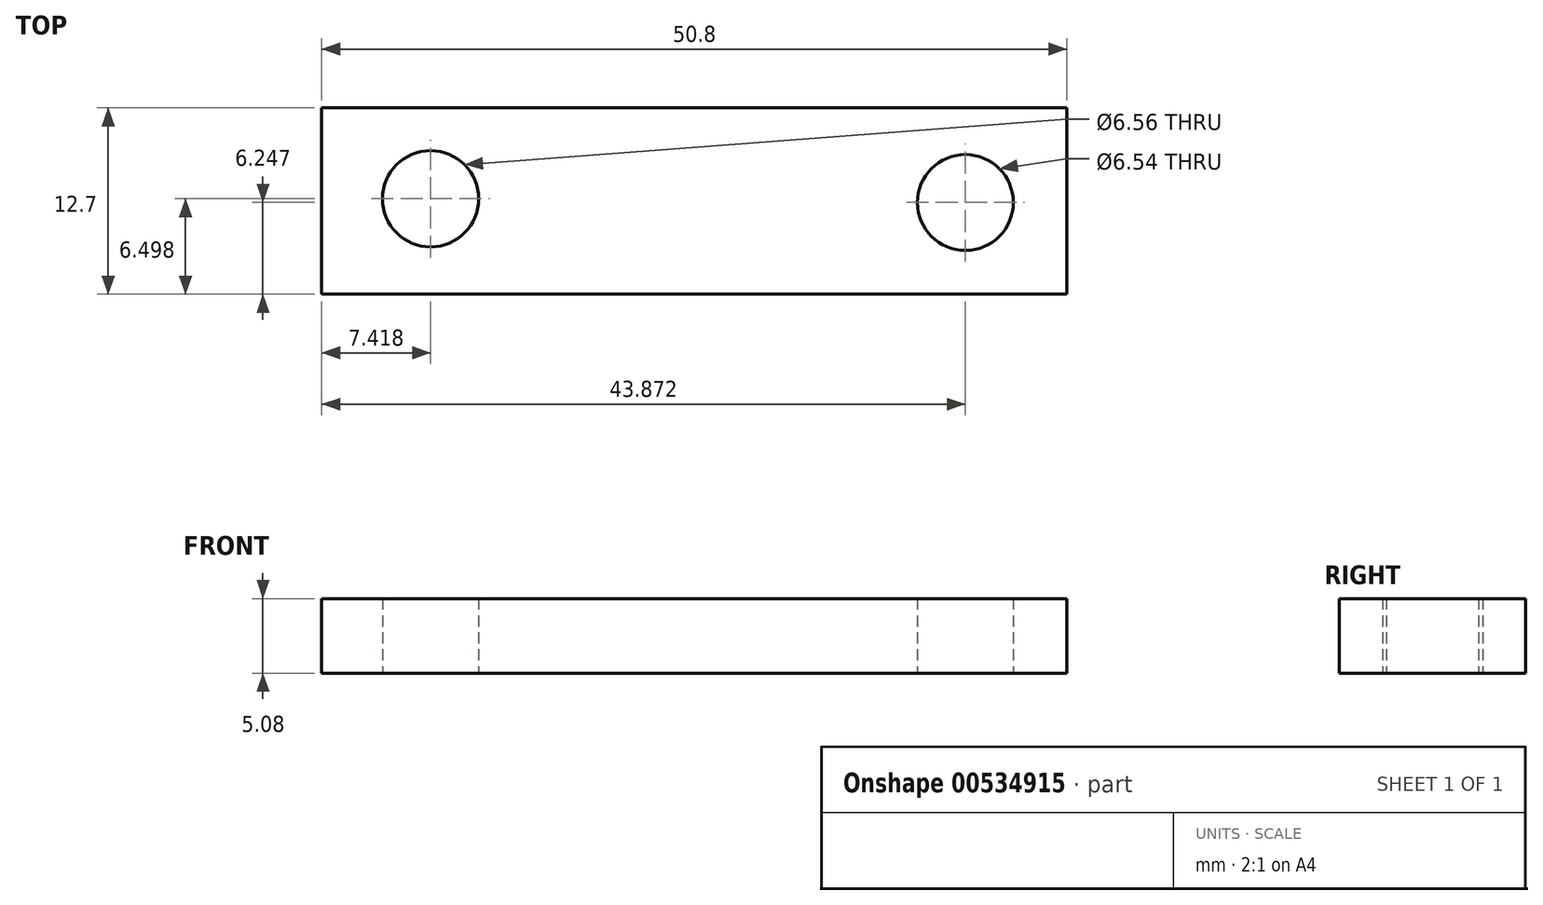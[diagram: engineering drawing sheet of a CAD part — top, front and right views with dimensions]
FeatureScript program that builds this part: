
annotation { "Feature Type Name" : "Feature", "Feature Type Description" : "" }
export const myFeature = defineFeature(function(context is Context, id is Id, definition is map)
    precondition{}
    {
        {
            var Q0;
            Q0=qCreatedBy(makeId("Top.planeOp"),FACE);
            var sketch = newSketch(context, id + "F0", { "sketchPlane" : qUnion([Q0])});
            skLineSegment(sketch, "E0.bottom", {"start": v(-28.41, 0) * mm, "end": v(22.39, 0) * mm});
            skLineSegment(sketch, "E0.top", {"start": v(-28.41, 12.7) * mm, "end": v(22.39, 12.7) * mm});
            skLineSegment(sketch, "E0.left", {"start": v(-28.41, 0) * mm, "end": v(-28.41, 12.7) * mm});
            skLineSegment(sketch, "E0.right", {"start": v(22.39, 0) * mm, "end": v(22.39, 12.7) * mm});
            skCircle(sketch, "E1", {"center": v(-21, 6.5) * mm, "radius": 3.28 * mm});
            skCircle(sketch, "E2", {"center": v(15.46, 6.25) * mm, "radius": 3.27 * mm});
            skSolve(sketch);
        }
        {
            var Q0;
            Q0=makeQuery(id+"F0.imprint","IMPRINT",FACE,{"disambiguationData":[TD([[makeQuery(id+"F0.imprint","IMPRINT",EDGE,{"derivedFrom":sQuery(id+"F0.wireOp",EDGE,"E0.bottom")}),1.0]])]});
            extrude(context, id + "F1", {"entities" : qUnion([Q0]), "depth" : 5.08 * mm, "offsetDistance" : 25.4 * mm});
        }
    });
